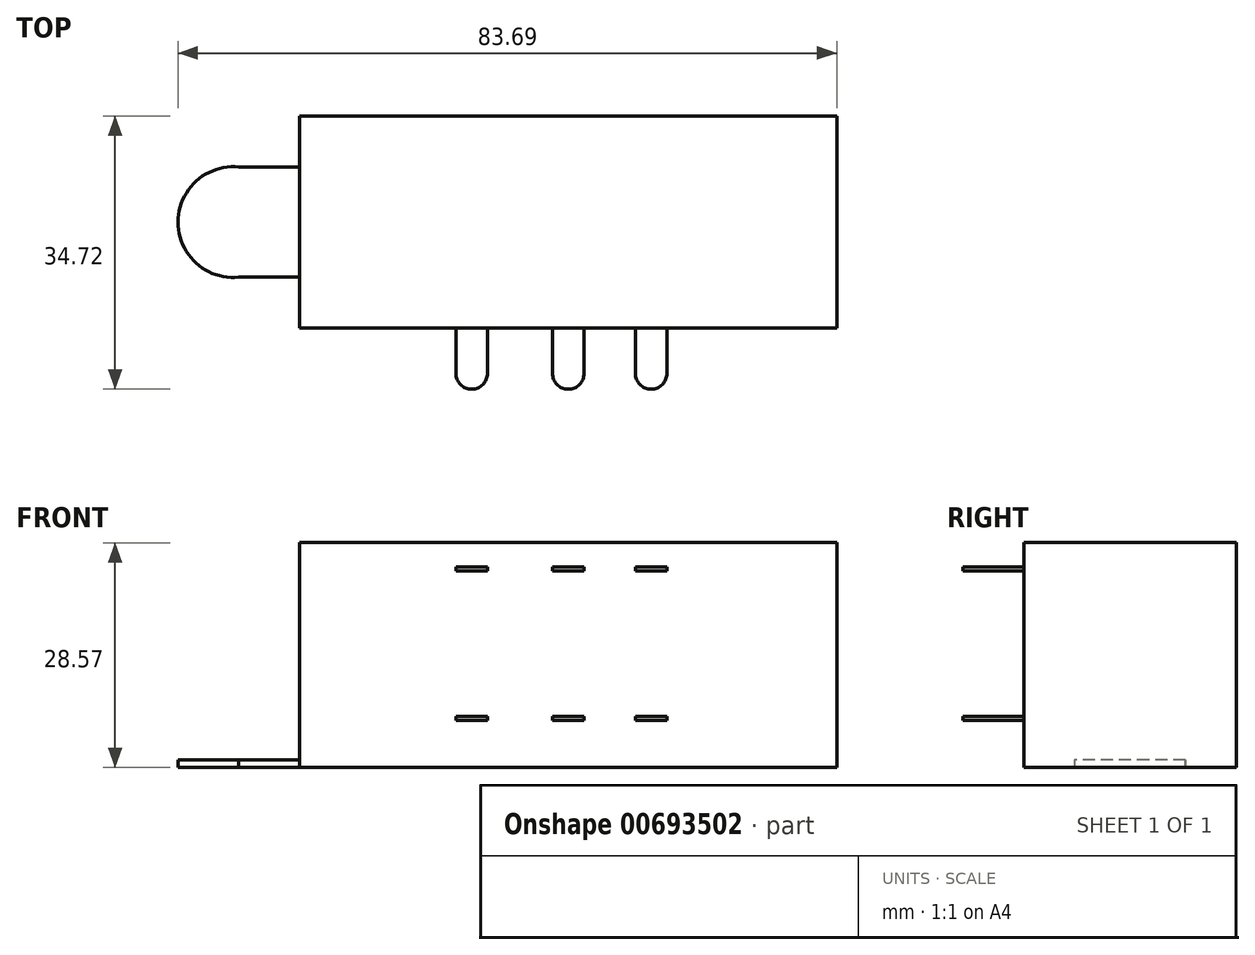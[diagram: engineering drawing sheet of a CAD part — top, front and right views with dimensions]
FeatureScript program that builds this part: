
annotation { "Feature Type Name" : "Feature", "Feature Type Description" : "" }
export const myFeature = defineFeature(function(context is Context, id is Id, definition is map)
    precondition{}
    {
        {
            var Q0;
            Q0=qCreatedBy(makeId("Right.planeOp"),FACE);
            var sketch = newSketch(context, id + "F0", { "sketchPlane" : qUnion([Q0])});
            skLineSegment(sketch, "E0", {"start": v(0, 0) * mm, "end": v(-13.49, 0) * mm});
            skLineSegment(sketch, "E1", {"start": v(-13.49, 0) * mm, "end": v(-13.49, 28.58) * mm});
            skLineSegment(sketch, "E2", {"start": v(-13.49, 28.58) * mm, "end": v(0, 28.58) * mm});
            skLineSegment(sketch, "E3.MirrorCS", {"start": v(0, 0) * mm, "end": v(13.49, 0) * mm});
            skLineSegment(sketch, "E4.MirrorCS", {"start": v(13.49, 0) * mm, "end": v(13.49, 28.58) * mm});
            skLineSegment(sketch, "E5.MirrorCS", {"start": v(13.49, 28.58) * mm, "end": v(0, 28.58) * mm});
            skSolve(sketch);
        }
        {
            var Q0;
            Q0 = qSketchRegion(id + "F0", true);
            extrude(context, id + "F1", {"entities" : qUnion([Q0]), "endBound" : BoundingType.SYMMETRIC, "depth" : 68.25 * mm, "offsetDistance" : 25 * mm});
        }
        {
            var Q0;
            Q0=qCreatedBy(makeId("Top.planeOp"),FACE);
            cPlane(context, id + "F2", {"entities" : qUnion([Q0]), "cplaneType" : CPlaneType.OFFSET, "offset" : 6 * mm, "width" : 150 * mm, "height" : 150 * mm});
        }
        {
            var Q0;
            Q0=qCreatedBy(makeId("Top.planeOp"),FACE);
            cPlane(context, id + "F3", {"entities" : qUnion([Q0]), "cplaneType" : CPlaneType.OFFSET, "offset" : 25 * mm, "width" : 150 * mm, "height" : 150 * mm});
        }
        {
            var Q0;
            Q0=qCreatedBy(id+"F2.planeOp",FACE);
            var sketch = newSketch(context, id + "F4", { "sketchPlane" : qUnion([Q0])});
            skCircle(sketch, "E6", {"center": v(0, -19.23) * mm, "radius": 2 * mm});
            skCircle(sketch, "E7", {"center": v(-12.27, -19.23) * mm, "radius": 2 * mm});
            skCircle(sketch, "E8", {"center": v(10.53, -19.23) * mm, "radius": 2 * mm});
            skLineSegment(sketch, "E9", {"start": v(-29.73, -19.23) * mm, "end": v(28.27, -19.23) * mm, "construction": true});
            skLineSegment(sketch, "E10", {"start": v(-14.27, -19.23) * mm, "end": v(-14.27, 0) * mm});
            skLineSegment(sketch, "E11", {"start": v(-10.27, -19.23) * mm, "end": v(-10.27, 0) * mm});
            skLineSegment(sketch, "E12", {"start": v(-2, -19.23) * mm, "end": v(-2, 0) * mm});
            skLineSegment(sketch, "E13", {"start": v(2, -19.23) * mm, "end": v(2, 0) * mm});
            skLineSegment(sketch, "E14", {"start": v(8.53, -19.23) * mm, "end": v(8.53, 0) * mm});
            skLineSegment(sketch, "E15", {"start": v(12.53, -19.23) * mm, "end": v(12.53, 0) * mm});
            skLineSegment(sketch, "E16", {"start": v(-14.27, 0) * mm, "end": v(-10.27, 0) * mm});
            skLineSegment(sketch, "E17", {"start": v(-2, 0) * mm, "end": v(2, 0) * mm});
            skLineSegment(sketch, "E18", {"start": v(8.53, 0) * mm, "end": v(12.53, 0) * mm});
            skSolve(sketch);
        }
        {
            var Q0;
            Q0 = qSketchRegion(id + "F4", true);
            extrude(context, id + "F5", {"entities" : qUnion([Q0]), "operationType" : NewBodyOperationType.ADD, "depth" : 0.5 * mm, "offsetDistance" : 25 * mm});
        }
        {
            var Q0;
            Q0=qCreatedBy(id+"F3.planeOp",FACE);
            var sketch = newSketch(context, id + "F6", { "sketchPlane" : qUnion([Q0])});
            skLineSegment(sketch, "E19.0.0", {"start": v(12.53, -19.23) * mm, "end": v(12.53, -13.49) * mm});
            skLineSegment(sketch, "E19.0.1", {"start": v(12.53, -13.49) * mm, "end": v(8.53, -13.49) * mm});
            skLineSegment(sketch, "E19.0.2", {"start": v(8.53, -13.49) * mm, "end": v(8.53, -19.23) * mm});
            skArc(sketch, "E19.0.3", {"start": v(8.53, -19.23) * mm, "mid": v(10.53, -21.23) * mm, "end": v(12.53, -19.23) * mm});
            skLineSegment(sketch, "E20.0.0", {"start": v(2, -19.23) * mm, "end": v(2, -13.49) * mm});
            skLineSegment(sketch, "E20.0.1", {"start": v(2, -13.49) * mm, "end": v(-2, -13.49) * mm});
            skLineSegment(sketch, "E20.0.2", {"start": v(-2, -13.49) * mm, "end": v(-2, -19.23) * mm});
            skArc(sketch, "E20.0.3", {"start": v(-2, -19.23) * mm, "mid": v(0, -21.23) * mm, "end": v(2, -19.23) * mm});
            skPoint(sketch, "E21.0", {"position": v(-10.27, -16.36) * mm});
            skLineSegment(sketch, "E22.0.0", {"start": v(-10.27, -19.23) * mm, "end": v(-10.27, -13.49) * mm});
            skLineSegment(sketch, "E22.0.1", {"start": v(-10.27, -13.49) * mm, "end": v(-14.27, -13.49) * mm});
            skLineSegment(sketch, "E22.0.2", {"start": v(-14.27, -13.49) * mm, "end": v(-14.27, -19.23) * mm});
            skArc(sketch, "E22.0.3", {"start": v(-14.27, -19.23) * mm, "mid": v(-12.27, -21.23) * mm, "end": v(-10.27, -19.23) * mm});
            skSolve(sketch);
        }
        {
            var Q0;
            Q0 = qSketchRegion(id + "F6", true);
            extrude(context, id + "F7", {"entities" : qUnion([Q0]), "operationType" : NewBodyOperationType.ADD, "depth" : 0.5 * mm, "offsetDistance" : 25 * mm});
        }
        {
            var Q0;
            Q0=qCreatedBy(makeId("Top.planeOp"),FACE);
            var sketch = newSketch(context, id + "F8", { "sketchPlane" : qUnion([Q0])});
            skLineSegment(sketch, "E23.0", {"start": v(-34.12, 13.49) * mm, "end": v(-34.12, -13.49) * mm});
            skCircle(sketch, "E24", {"center": v(-42.53, 0) * mm, "radius": 7.04 * mm});
            skLineSegment(sketch, "E25", {"start": v(-41.87, -7) * mm, "end": v(-28.3, -7) * mm});
            skLineSegment(sketch, "E26", {"start": v(-41.85, 7) * mm, "end": v(-29.15, 7) * mm});
            skLineSegment(sketch, "E27", {"start": v(-28.3, -7) * mm, "end": v(-29.15, 7) * mm});
            skSolve(sketch);
        }
        {
            var Q0;
            Q0 = qSketchRegion(id + "F8", true);
            extrude(context, id + "F9", {"entities" : qUnion([Q0]), "operationType" : NewBodyOperationType.ADD, "depth" : 1 * mm, "offsetDistance" : 25 * mm});
        }
    });
